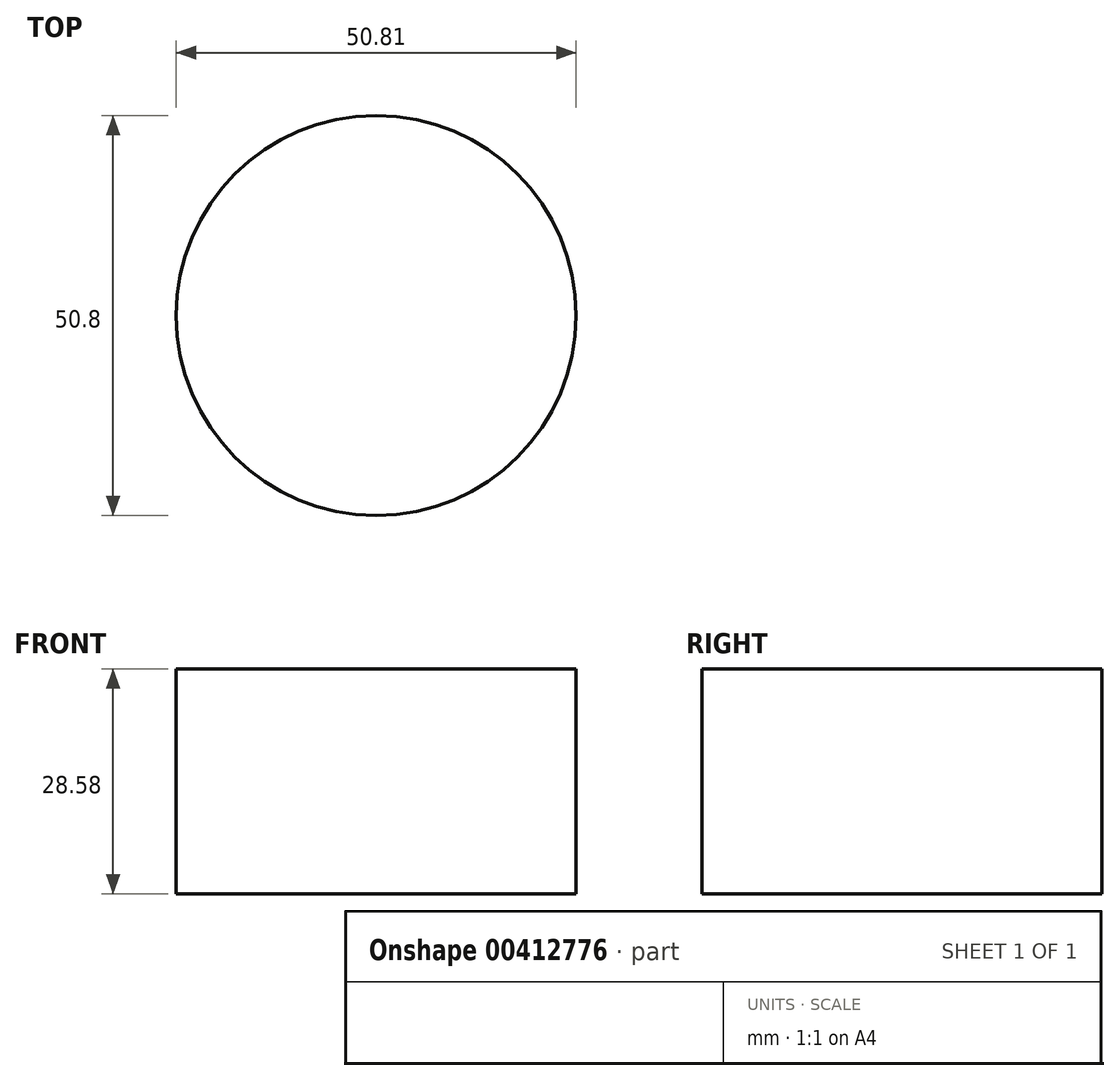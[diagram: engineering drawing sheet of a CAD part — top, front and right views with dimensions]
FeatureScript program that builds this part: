
annotation { "Feature Type Name" : "Feature", "Feature Type Description" : "" }
export const myFeature = defineFeature(function(context is Context, id is Id, definition is map)
    precondition{}
    {
        {
            var Q0;
            Q0=qCreatedBy(makeId("Front.planeOp"),FACE);
            var sketch = newSketch(context, id + "F0", { "sketchPlane" : qUnion([Q0])});
            skLineSegment(sketch, "E0.bottom", {"start": v(41.28, -9.52) * mm, "end": v(-41.28, -9.53) * mm});
            skLineSegment(sketch, "E0.top", {"start": v(41.28, 9.53) * mm, "end": v(-41.28, 9.52) * mm});
            skLineSegment(sketch, "E0.left", {"start": v(41.28, -9.52) * mm, "end": v(41.28, 9.53) * mm});
            skLineSegment(sketch, "E0.right", {"start": v(-41.28, -9.53) * mm, "end": v(-41.28, 9.52) * mm});
            skPoint(sketch, "E0.middle", {"position": v(0, 0) * mm});
            skLineSegment(sketch, "E1.bottom", {"start": v(111.12, 38.1) * mm, "end": v(60.32, 38.1) * mm});
            skLineSegment(sketch, "E1.top", {"start": v(111.12, 66.68) * mm, "end": v(60.32, 66.68) * mm});
            skLineSegment(sketch, "E1.left", {"start": v(111.12, 38.1) * mm, "end": v(111.12, 66.68) * mm});
            skLineSegment(sketch, "E1.right", {"start": v(60.32, 38.1) * mm, "end": v(60.32, 66.68) * mm});
            skPoint(sketch, "E1.middle", {"position": v(85.72, 52.39) * mm});
            skLineSegment(sketch, "E2", {"start": v(41.28, 9.53) * mm, "end": v(41.28, 27) * mm});
            skArc(sketch, "E3", {"start": v(41.28, 27) * mm, "mid": v(45.92, 38.23) * mm, "end": v(57.15, 42.88) * mm});
            skLineSegment(sketch, "E4", {"start": v(57.15, 42.88) * mm, "end": v(79.62, 42.88) * mm});
            skLineSegment(sketch, "E5.0", {"start": v(57.15, 61.93) * mm, "end": v(79.62, 61.93) * mm});
            skArc(sketch, "E5.1", {"start": v(22.23, 27) * mm, "mid": v(32.45, 51.7) * mm, "end": v(57.15, 61.93) * mm});
            skLineSegment(sketch, "E5.2", {"start": v(22.23, 9.53) * mm, "end": v(22.23, 27) * mm});
            skFitSpline(sketch, "E6", {"points": [v(60.32, 61.93) * mm, v(-41.28, 9.52) * mm], "startDerivative": vector(-237.5, 3.05) * mm, "endDerivative": vector(-16.74, -81.16) * mm});
            skLineSegment(sketch, "E7", {"start": v(85.72, 66.68) * mm, "end": v(85.72, 38.1) * mm});
            skSolve(sketch);
        }
        {
            var Q0;
            Q0=makeQuery(id+"F0.imprint","IMPRINT",FACE,{"disambiguationData":[TD([[makeQuery(id+"F0.imprint","IMPRINT",EDGE,{"derivedFrom":sQuery(id+"F0.wireOp",EDGE,"E0.bottom")}),-1.0]])]});
            extrude(context, id + "F1", {"entities" : qUnion([Q0]), "endBound" : BoundingType.SYMMETRIC, "depth" : 127 * mm});
        }
        {
            var Q0;
            {var subQ6=sQuery(id+"F0.wireOp",EDGE,"E7");Q0=makeQuery(id+"F0.imprint","IMPRINT",FACE,{"disambiguationData":[TD([[makeQuery(id+"F0.imprint","IMPRINT",EDGE,{"derivedFrom":subQ6}),-1.0]])]});}
            var Q1;
            {var subQ1=sQuery(id+"F0.wireOp",EDGE,"E2");Q1=makeQuery(id+"F0.imprint","IMPRINT",FACE,{"disambiguationData":[TD([[makeQuery(id+"F0.imprint","IMPRINT",EDGE,{"derivedFrom":subQ1}),1.0]])]});}
            var Q2;
            {var subQ0=sQuery(id+"F0.wireOp",EDGE,"E1.left");Q2=makeQuery(id+"F0.imprint","IMPRINT",FACE,{"disambiguationData":[TD([[makeQuery(id+"F0.imprint","IMPRINT",EDGE,{"derivedFrom":subQ0}),1.0]])]});}
            extrude(context, id + "F2", {"entities" : qUnion([Q0, Q1, Q2]), "operationType" : NewBodyOperationType.ADD, "endBound" : BoundingType.SYMMETRIC, "depth" : 50.8 * mm});
        }
        {
            var Q0;
            {var subQ0=sQuery(id+"F0.wireOp",EDGE,"E5.1");Q0=makeQuery(id+"F0.imprint","IMPRINT",FACE,{"disambiguationData":[TD([[makeQuery(id+"F0.imprint","IMPRINT",EDGE,{"derivedFrom":subQ0}),1.0]])]});}
            extrude(context, id + "F3", {"entities" : qUnion([Q0]), "operationType" : NewBodyOperationType.ADD, "endBound" : BoundingType.SYMMETRIC, "depth" : 15.88 * mm});
        }
        {
            var Q0;
            {var subQ0=sQuery(id+"F0.wireOp",EDGE,"E1.left");Q0=makeQuery(id+"F0.imprint","IMPRINT",FACE,{"disambiguationData":[TD([[makeQuery(id+"F0.imprint","IMPRINT",EDGE,{"derivedFrom":subQ0}),1.0]])]});}
            var Q1;
            Q1=sQuery(id+"F0.wireOp",EDGE,"E7");
            revolve(context, id + "F4", {"operationType" : NewBodyOperationType.INTERSECT, "entities" : qUnion([Q0]), "axis" : qUnion([Q1]), "revolveType" : RevolveType.FULL});
        }
    });
